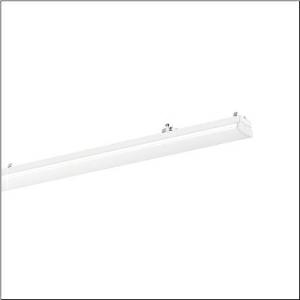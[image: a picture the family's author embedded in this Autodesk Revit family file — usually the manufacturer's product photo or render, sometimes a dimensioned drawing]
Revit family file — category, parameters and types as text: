
# Revit family: licross_21_recessed_opal_mo_52tl1d7n44xg
name_source: partatom
category: Lighting Fixtures
units: mm (PartAtom-declared; Revit-internal decimal feet)

## family parameters
Cut with Voids When Loaded = No
Host = Face
Light Source = No
Part Type = Normal
Room Calculation Point = No
Round Connector Dimension = Use Diameter
Shared = No

## types (1)
- Licross 21 recessed opal MO (1 x LED, 4400 lm, 24.7 W, 4000K)
    Apparent Load = 25 VA
    CIE Flux Codes = 44 73 91 87 100
    Color Rendering = 80
    Color Temperature = 4000K
    Default Elevation = 1800 mm
    Description = Licross 21 recessed opal MO, luminaire insert, of sheet steel, galvanised, coil coated, white, length: 1.500mm, width: 66mm, height: 67mm, LED rated luminous flux: 4.400lm, light colour: 840, SDCM (Standard Deviation of Colour Matching)MacAdam ≤ 3 SDCM (initial), control gear: ON/OFF, with plug, 3-pole, with phase selection, mains connection: 220..240V, AC, 50/60Hz, rated input power: 25W, internal wiring halogen-free, primary optical cover: cover, of PMMA, light emission: direct with ceiling illumination distribution, primary light characteristic: symmetric, protection rating (complete): IP40, insulation class (complete): insulation class I (protective earthing), certification: CE, ENEC, VDE, UKCA, protection symbol: D if used in an environment without relevant dust loads with corresponding accessories, impact resistance: IK06, permissible ambient temperature for indoor applications: -35..+50°C, corresponds to IFS (International Featured Standards) requirements for safety and quality in the food industry, reducing of maximum allowable ambient temperature of 5°C with ceiling mounting, LABS conformity tested according to VDMA 24364:2018-05, The light source and the operating device comply with the requirements of the Ecodesign Regulation (EU) 2019/2020 and are replaceable in accordance with this regulation, packaging unit: 1 piece
    Height = 83 mm
    Lamp = 1 x LED
    Lamp Light Flux = 4400 lm
    Lamp Power = 24.7 W
    Lamp count = 1
    Length = 1500 mm
    Luminous efficacy = 178 lm/W
    Manufacturer = Siteco
    ModVariant = No
    Model = 52TL1D7N44XG
    Mounting Place = Ceiling
    Mounting Type = Pendant
    Number of Poles = 1
    OnlyDefault = Yes
    Power Factor = 1
    Product Name = Licross 21 recessed opal MO
    Product group = luminaire insert | ceiling pendant
    ProductGroupID = 901
    Protection Class = Protection class I
    Protection Degree = IP 40
    RLX_Detail_Level = 1
    RLX_Emergency_Light_Flux = 0 lm
    RLX_Emergency_Type = 0
    RLX_Emergency_Type_DB = No
    RlxData = <blob elided: 23381 chars, md5=be0f3a2d>
    Socket = socket
    Standby Power = 0 W
    System Light Flux = 4400 lm
    System Power = 25 W
    Type Comments = Product without accessories
    Type Image = l_1313666.jpg
    URL = http://relux.com
    VarID = ---
    Voltage = 0 V
    Weight = 0.00 kg
    Width = 76 mm

## geometry (parser evidence)
native form markers: Blend x4, Sweep x13
no freeform markers — native parametric forms only
